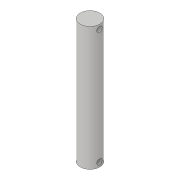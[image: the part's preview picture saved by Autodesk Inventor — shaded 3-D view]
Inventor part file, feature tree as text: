
AUTODESK INVENTOR PART (.ipt)
format: ipt  version: 2019.4 (Build 234330000, 330)  size: 80,384 bytes
history: native  units: in
note: dims shown in document units (in); Inventor stores cm internally (conversion verified against a paired STEP export)
features: sketch x2, extrude x1, hole x1
ambient origin geometry x8: Origin, YZ Plane, XZ Plane, XY Plane, X Axis, Y Axis, Z Axis, Center Point
bodies: Solid1 (feature_tree)
feature tree (4):
  extrude  "Extrusion1"  Depth=4.252in TaperAngle=0.0deg
  hole  "Hole1"  [1 undecoded]
  sketch  "Sketch1"  dims[d0=0.6693in d1=4.252in d2=0.0in]
  sketch  "Sketch2"  dims[d3=3.937in d4=0.1875in d5=0.75in d6=0.75in d7=0.188in d8=0.5635in d9=1.0in d10=0.8108in]
note: 1 required parameter value undecoded (feature->parameter linkage not recoverable at this tier; creation-order binding heuristic only, values carry confidence <= 0.55)
